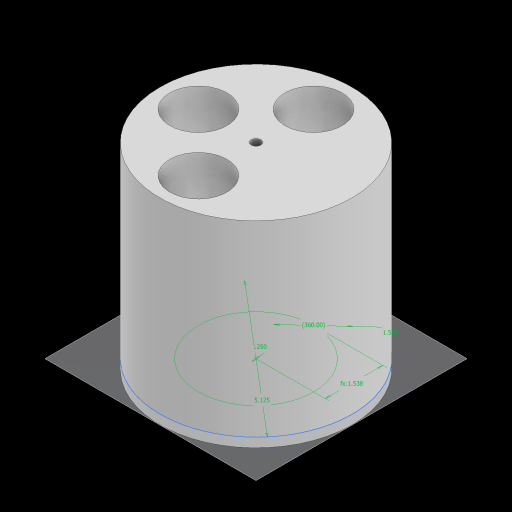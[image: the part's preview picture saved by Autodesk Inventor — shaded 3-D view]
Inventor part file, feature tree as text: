
AUTODESK INVENTOR PART (.ipt)
format: ipt  version: 2023 (Build 270158000, 158)  size: 133,120 bytes
history: native  units: in
note: dims shown in document units (in); Inventor stores cm internally (conversion verified against a paired STEP export)
features: sketch x2, extrude x2, plane x1
ambient origin geometry x8: Origin, YZ Plane, XZ Plane, XY Plane, X Axis, Y Axis, Z Axis, Center Point
bodies: Solid1 (feature_tree)
feature tree (5):
  sketch  "Sketch2"  dims[d2=5.125in d3=1.525in]
  extrude  "Extrusion1"  Depth=1.525in
  extrude  "Extrusion2"  Depth=2.5625in TaperAngle=360.0deg
  plane  "Work Plane1"
  sketch  "Sketch3"  dims[d5=1.5375in d6=1.5748in d8=360.0deg d10=5.0in d11=0.0in d12=0.25in d13=0.0in d14=0.25in d15=2.5625in d16=0.1in d17=1.0in]
